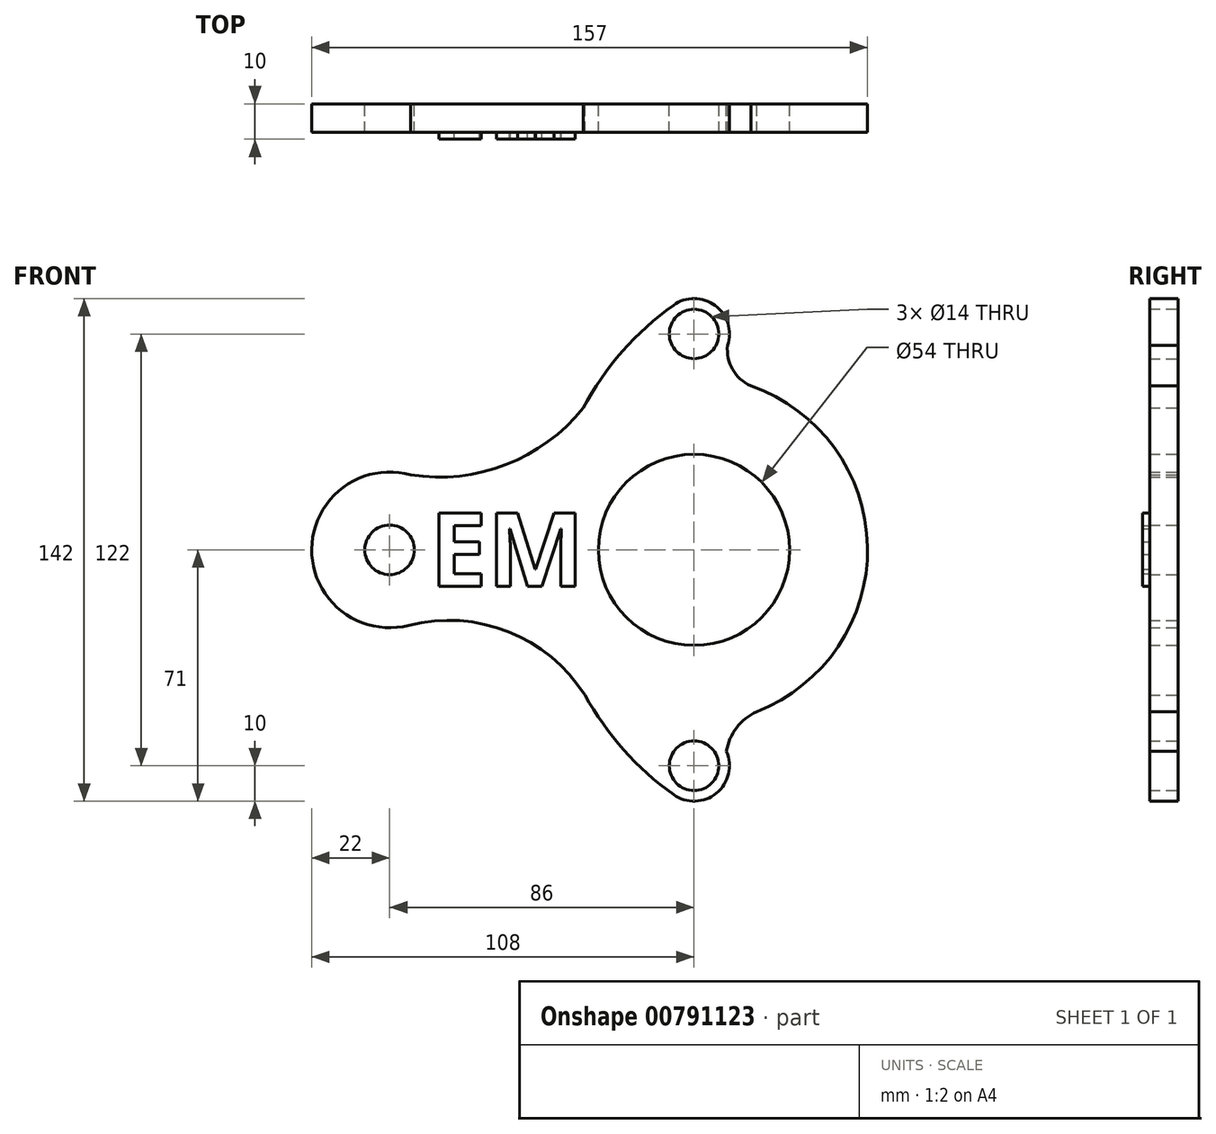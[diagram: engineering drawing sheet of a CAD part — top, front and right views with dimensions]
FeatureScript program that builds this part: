
annotation { "Feature Type Name" : "Feature", "Feature Type Description" : "" }
export const myFeature = defineFeature(function(context is Context, id is Id, definition is map)
    precondition{}
    {
        {
            var Q0;
            Q0=qCreatedBy(makeId("Front.planeOp"),FACE);
            var sketch = newSketch(context, id + "F0", { "sketchPlane" : qUnion([Q0])});
            skArc(sketch, "E0", {"start": v(17.68, -45.7) * mm, "mid": v(49, 0.88) * mm, "end": v(16.04, 46.3) * mm});
            skCircle(sketch, "E1", {"center": v(0, 0) * mm, "radius": 27 * mm});
            skLineSegment(sketch, "E2", {"start": v(0, 0) * mm, "end": v(-86, 0) * mm});
            skLineSegment(sketch, "E3", {"start": v(0, 0) * mm, "end": v(0, 61) * mm});
            skLineSegment(sketch, "E4", {"start": v(0, 0) * mm, "end": v(0, -61) * mm});
            skCircle(sketch, "E5", {"center": v(0, 61) * mm, "radius": 7 * mm});
            skCircle(sketch, "E6", {"center": v(0, 61) * mm, "radius": 10 * mm});
            skCircle(sketch, "E7", {"center": v(0, -61) * mm, "radius": 7 * mm});
            skCircle(sketch, "E8", {"center": v(0, -61) * mm, "radius": 10 * mm});
            skCircle(sketch, "E9", {"center": v(-86, 0) * mm, "radius": 7 * mm});
            skArc(sketch, "E10", {"start": v(-80.02, 21.17) * mm, "mid": v(-108, 0.3) * mm, "end": v(-80.59, -21.32) * mm});
            skArc(sketch, "E11", {"start": v(-5.82, 69.13) * mm, "mid": v(-20.25, 56.07) * mm, "end": v(-31.33, 40.06) * mm});
            skArc(sketch, "E12", {"start": v(-80.02, 21.17) * mm, "mid": v(-53.13, 24.05) * mm, "end": v(-31.33, 40.06) * mm});
            skArc(sketch, "E13", {"start": v(-30.78, -41.08) * mm, "mid": v(-52.49, -23.14) * mm, "end": v(-80.59, -21.32) * mm});
            skArc(sketch, "E14", {"start": v(9.46, 57.76) * mm, "mid": v(10.91, 50.98) * mm, "end": v(16.04, 46.3) * mm});
            skArc(sketch, "E15", {"start": v(17.68, -45.7) * mm, "mid": v(12.01, -50.25) * mm, "end": v(9.13, -56.93) * mm});
            skArc(sketch, "E16.trimOffspring", {"start": v(-30.78, -41.08) * mm, "mid": v(-19.87, -56.5) * mm, "end": v(-5.82, -69.13) * mm});
            skSolve(sketch);
        }
        {
            var Q0;
            Q0=makeQuery(id+"F0.imprint","IMPRINT",FACE,{"disambiguationData":[TD([[makeQuery(id+"F0.imprint","IMPRINT",EDGE,{"derivedFrom":sQuery(id+"F0.wireOp",EDGE,"E9")}),-1.0]])]});
            var Q1;
            Q1=makeQuery(id+"F0.imprint","IMPRINT",FACE,{"disambiguationData":[TD([[makeQuery(id+"F0.imprint","IMPRINT",EDGE,{"derivedFrom":sQuery(id+"F0.wireOp",EDGE,"E0")}),1.0]])]});
            var Q2;
            Q2=makeQuery(id+"F0.imprint","IMPRINT",FACE,{"disambiguationData":[TD([[makeQuery(id+"F0.imprint","IMPRINT",EDGE,{"derivedFrom":sQuery(id+"F0.wireOp",EDGE,"E7")}),-1.0]])]});
            var Q3;
            Q3=makeQuery(id+"F0.imprint","IMPRINT",FACE,{"disambiguationData":[TD([[makeQuery(id+"F0.imprint","IMPRINT",EDGE,{"derivedFrom":sQuery(id+"F0.wireOp",EDGE,"E5")}),-1.0]])]});
            extrude(context, id + "F1", {"entities" : qUnion([Q0, Q1, Q2, Q3]), "depth" : 8 * mm, "offsetDistance" : 25 * mm});
        }
        {
            var Q0;
            Q0=makeQuery(id+"F1.opExtrude","CAP_FACE",FACE,{"disambiguationData":[OSD([sQuery(id+"F0.wireOp",EDGE,"E0"),sQuery(id+"F0.wireOp",EDGE,"E1"),sQuery(id+"F0.wireOp",EDGE,"E5"),sQuery(id+"F0.wireOp",EDGE,"E6"),sQuery(id+"F0.wireOp",EDGE,"E7"),sQuery(id+"F0.wireOp",EDGE,"E8"),sQuery(id+"F0.wireOp",EDGE,"E9"),sQuery(id+"F0.wireOp",EDGE,"E10"),sQuery(id+"F0.wireOp",EDGE,"E11"),sQuery(id+"F0.wireOp",EDGE,"E12"),sQuery(id+"F0.wireOp",EDGE,"E13"),sQuery(id+"F0.wireOp",EDGE,"E14"),sQuery(id+"F0.wireOp",EDGE,"E15"),sQuery(id+"F0.wireOp",EDGE,"E16.trimOffspring")])],"isStart":false});
            var sketch = newSketch(context, id + "F2", { "sketchPlane" : qUnion([Q0])});
            skText(sketch, "E17", { "text": "EM", "fontName": "OpenSans-Bold.ttf"});
            const initialGuessF2  = {"E17": [-0.07471, -0.01034, 1, 0, 0.02096]};
            skSetInitialGuess(sketch, initialGuessF2);
            skSolve(sketch);
        }
        {
            var Q0;
            Q0 = qSketchRegion(id + "F2", true);
            extrude(context, id + "F3", {"entities" : qUnion([Q0]), "operationType" : NewBodyOperationType.ADD, "depth" : 2 * mm, "offsetDistance" : 25 * mm});
        }
    });
